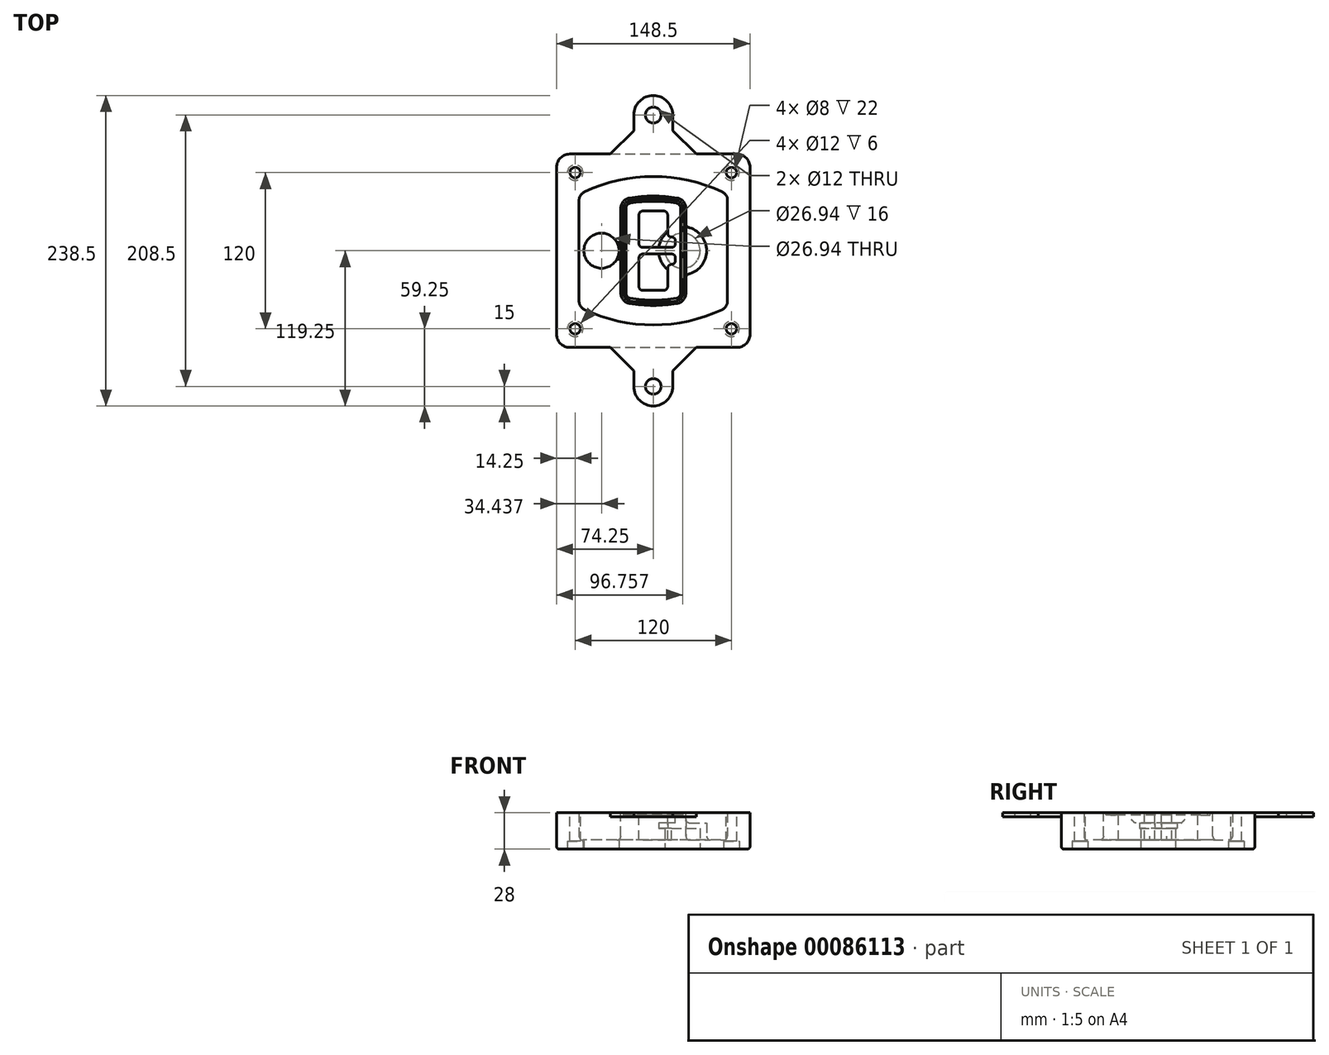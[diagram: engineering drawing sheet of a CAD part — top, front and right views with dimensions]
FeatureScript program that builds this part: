
annotation { "Feature Type Name" : "Feature", "Feature Type Description" : "" }
export const myFeature = defineFeature(function(context is Context, id is Id, definition is map)
    precondition{}
    {
        {
            var Q0;
            Q0=qCreatedBy(makeId("Top.planeOp"),FACE);
            var sketch = newSketch(context, id + "F0", { "sketchPlane" : qUnion([Q0])});
            skPoint(sketch, "E0.rect.middle", {"position": v(0, 0) * mm});
            skLineSegment(sketch, "E1.bottom", {"start": v(-64.25, -74.25) * mm, "end": v(64.25, -74.25) * mm});
            skLineSegment(sketch, "E1.top", {"start": v(-64.25, 74.25) * mm, "end": v(64.25, 74.25) * mm});
            skLineSegment(sketch, "E1.left", {"start": v(-74.25, -64.25) * mm, "end": v(-74.25, 64.25) * mm});
            skLineSegment(sketch, "E1.right", {"start": v(74.25, -64.25) * mm, "end": v(74.25, 64.25) * mm});
            skLineSegment(sketch, "E2", {"start": v(-74.25, 74.25) * mm, "end": v(74.25, -74.25) * mm, "construction": true});
            skLineSegment(sketch, "E3", {"start": v(74.25, 74.25) * mm, "end": v(-74.25, -74.25) * mm, "construction": true});
            skCircle(sketch, "E4", {"center": v(-60, 60) * mm, "radius": 4 * mm});
            skCircle(sketch, "E5", {"center": v(60, 60) * mm, "radius": 4 * mm});
            skCircle(sketch, "E6", {"center": v(60, -60) * mm, "radius": 4 * mm});
            skCircle(sketch, "E7", {"center": v(-60, -60) * mm, "radius": 4 * mm});
            skLineSegment(sketch, "E8", {"start": v(-60, 60) * mm, "end": v(60, 60) * mm, "construction": true});
            skLineSegment(sketch, "E9", {"start": v(60, 60) * mm, "end": v(60, -60) * mm, "construction": true});
            skLineSegment(sketch, "E10", {"start": v(60, -60) * mm, "end": v(-60, -60) * mm, "construction": true});
            skLineSegment(sketch, "E11", {"start": v(-60, -60) * mm, "end": v(-60, 60) * mm, "construction": true});
            skLineSegment(sketch, "E12", {"start": v(-60, 38.83) * mm, "end": v(-60, -38.83) * mm});
            skLineSegment(sketch, "E13", {"start": v(60, 38.83) * mm, "end": v(60, -38.83) * mm});
            skArc(sketch, "E14", {"start": v(54.26, 47.88) * mm, "mid": v(0, 60) * mm, "end": v(-54.26, 47.88) * mm});
            skArc(sketch, "E15", {"start": v(-54.26, -47.88) * mm, "mid": v(0, -60) * mm, "end": v(54.26, -47.88) * mm});
            skLineSegment(sketch, "E16", {"start": v(-60, 0) * mm, "end": v(60, 0) * mm, "construction": true});
            skPoint(sketch, "E17.visualSharp", {"position": v(-60, -45) * mm});
            skArc(sketch, "E17.filletArc", {"start": v(-60, -38.83) * mm, "mid": v(-58.44, -44.2) * mm, "end": v(-54.26, -47.88) * mm});
            skPoint(sketch, "E18.visualSharp", {"position": v(-60, 45) * mm});
            skArc(sketch, "E18.filletArc", {"start": v(-54.26, 47.88) * mm, "mid": v(-58.44, 44.2) * mm, "end": v(-60, 38.83) * mm});
            skPoint(sketch, "E19.visualSharp", {"position": v(60, 45) * mm});
            skArc(sketch, "E19.filletArc", {"start": v(60, 38.83) * mm, "mid": v(58.44, 44.2) * mm, "end": v(54.26, 47.88) * mm});
            skPoint(sketch, "E20.visualSharp", {"position": v(60, -45) * mm});
            skArc(sketch, "E20.filletArc", {"start": v(54.26, -47.88) * mm, "mid": v(58.44, -44.2) * mm, "end": v(60, -38.83) * mm});
            skPoint(sketch, "E21.visualSharp", {"position": v(-74.25, 74.25) * mm});
            skArc(sketch, "E21.filletArc", {"start": v(-64.25, 74.25) * mm, "mid": v(-71.32, 71.32) * mm, "end": v(-74.25, 64.25) * mm});
            skPoint(sketch, "E22.visualSharp", {"position": v(74.25, 74.25) * mm});
            skArc(sketch, "E22.filletArc", {"start": v(74.25, 64.25) * mm, "mid": v(71.32, 71.32) * mm, "end": v(64.25, 74.25) * mm});
            skPoint(sketch, "E23.visualSharp", {"position": v(74.25, -74.25) * mm});
            skArc(sketch, "E23.filletArc", {"start": v(64.25, -74.25) * mm, "mid": v(71.32, -71.32) * mm, "end": v(74.25, -64.25) * mm});
            skPoint(sketch, "E24.visualSharp", {"position": v(-74.25, -74.25) * mm});
            skArc(sketch, "E24.filletArc", {"start": v(-74.25, -64.25) * mm, "mid": v(-71.32, -71.32) * mm, "end": v(-64.25, -74.25) * mm});
            skArc(sketch, "E25.0", {"start": v(57, 38.83) * mm, "mid": v(55.9, 42.58) * mm, "end": v(52.98, 45.17) * mm});
            skLineSegment(sketch, "E25.1", {"start": v(57, 38.83) * mm, "end": v(57, -38.83) * mm});
            skArc(sketch, "E25.2", {"start": v(52.98, -45.17) * mm, "mid": v(55.9, -42.58) * mm, "end": v(57, -38.83) * mm});
            skArc(sketch, "E25.3", {"start": v(-52.98, -45.17) * mm, "mid": v(0, -57) * mm, "end": v(52.98, -45.17) * mm});
            skArc(sketch, "E25.4", {"start": v(-57, -38.83) * mm, "mid": v(-55.9, -42.58) * mm, "end": v(-52.98, -45.17) * mm});
            skArc(sketch, "E25.5", {"start": v(52.98, 45.17) * mm, "mid": v(0, 57) * mm, "end": v(-52.98, 45.17) * mm});
            skLineSegment(sketch, "E25.6", {"start": v(-57, 38.83) * mm, "end": v(-57, -38.83) * mm});
            skArc(sketch, "E25.7", {"start": v(-52.98, 45.17) * mm, "mid": v(-55.9, 42.58) * mm, "end": v(-57, 38.83) * mm});
            skArc(sketch, "E26.0", {"start": v(-55.96, 51.5) * mm, "mid": v(-61.82, 46.33) * mm, "end": v(-64, 38.83) * mm});
            skArc(sketch, "E26.1", {"start": v(55.96, 51.5) * mm, "mid": v(0, 64) * mm, "end": v(-55.96, 51.5) * mm});
            skArc(sketch, "E26.2", {"start": v(64, 38.83) * mm, "mid": v(61.82, 46.33) * mm, "end": v(55.96, 51.5) * mm});
            skLineSegment(sketch, "E26.3", {"start": v(64, 38.83) * mm, "end": v(64, -38.83) * mm});
            skArc(sketch, "E26.4", {"start": v(55.96, -51.5) * mm, "mid": v(61.82, -46.33) * mm, "end": v(64, -38.83) * mm});
            skLineSegment(sketch, "E26.5", {"start": v(-64, 38.83) * mm, "end": v(-64, -38.83) * mm});
            skArc(sketch, "E26.6", {"start": v(-55.96, -51.5) * mm, "mid": v(0, -64) * mm, "end": v(55.96, -51.5) * mm});
            skArc(sketch, "E26.7", {"start": v(-64, -38.83) * mm, "mid": v(-61.82, -46.33) * mm, "end": v(-55.96, -51.5) * mm});
            skSolve(sketch);
        }
        {
            var Q0;
            Q0=makeQuery(id+"F0.imprint","IMPRINT",FACE,{"disambiguationData":[TD([[makeQuery(id+"F0.imprint","IMPRINT",EDGE,{"derivedFrom":sQuery(id+"F0.wireOp",EDGE,"E1.bottom")}),1.0]])]});
            var Q1;
            Q1=makeQuery(id+"F0.imprint","IMPRINT",FACE,{"disambiguationData":[TD([[makeQuery(id+"F0.imprint","IMPRINT",EDGE,{"derivedFrom":sQuery(id+"F0.wireOp",EDGE,"E12")}),1.0]])]});
            var Q2;
            Q2=makeQuery(id+"F0.imprint","IMPRINT",FACE,{"disambiguationData":[TD([[makeQuery(id+"F0.imprint","IMPRINT",EDGE,{"derivedFrom":sQuery(id+"F0.wireOp",EDGE,"E25.0")}),1.0]])]});
            var Q3;
            Q3=makeQuery(id+"F0.imprint","IMPRINT",FACE,{"disambiguationData":[TD([[makeQuery(id+"F0.imprint","IMPRINT",EDGE,{"derivedFrom":sQuery(id+"F0.wireOp",EDGE,"E12")}),-1.0]])]});
            extrude(context, id + "F1", {"entities" : qUnion([Q0, Q1, Q2, Q3]), "oppositeDirection" : true, "depth" : 25 * mm});
        }
        {
            var Q0;
            Q0=makeQuery(id+"F0.imprint","IMPRINT",FACE,{"disambiguationData":[TD([[makeQuery(id+"F0.imprint","IMPRINT",EDGE,{"derivedFrom":sQuery(id+"F0.wireOp",EDGE,"E12")}),1.0]])]});
            extrude(context, id + "F2", {"entities" : qUnion([Q0]), "operationType" : NewBodyOperationType.ADD, "depth" : 3 * mm});
        }
        {
            var Q0;
            Q0=makeQuery(id+"F0.imprint","IMPRINT",FACE,{"disambiguationData":[TD([[makeQuery(id+"F0.imprint","IMPRINT",EDGE,{"derivedFrom":sQuery(id+"F0.wireOp",EDGE,"E25.0")}),1.0]])]});
            extrude(context, id + "F3", {"entities" : qUnion([Q0]), "operationType" : NewBodyOperationType.REMOVE, "oppositeDirection" : true, "depth" : 18 * mm});
        }
        {
            var Q0;
            Q0=makeQuery(id+"F2.opExtrude","CAP_FACE",FACE,{"disambiguationData":[OSD([sQuery(id+"F0.wireOp",EDGE,"E12"),sQuery(id+"F0.wireOp",EDGE,"E13"),sQuery(id+"F0.wireOp",EDGE,"E14"),sQuery(id+"F0.wireOp",EDGE,"E15"),sQuery(id+"F0.wireOp",EDGE,"E17.filletArc"),sQuery(id+"F0.wireOp",EDGE,"E18.filletArc"),sQuery(id+"F0.wireOp",EDGE,"E19.filletArc"),sQuery(id+"F0.wireOp",EDGE,"E20.filletArc"),sQuery(id+"F0.wireOp",EDGE,"E25.0"),sQuery(id+"F0.wireOp",EDGE,"E25.1"),sQuery(id+"F0.wireOp",EDGE,"E25.2"),sQuery(id+"F0.wireOp",EDGE,"E25.3"),sQuery(id+"F0.wireOp",EDGE,"E25.4"),sQuery(id+"F0.wireOp",EDGE,"E25.5"),sQuery(id+"F0.wireOp",EDGE,"E25.6"),sQuery(id+"F0.wireOp",EDGE,"E25.7")])],"isStart":false});
            var sketch = newSketch(context, id + "F4", { "sketchPlane" : qUnion([Q0])});
            skArc(sketch, "E27.0", {"start": v(-18.34, -40.45) * mm, "mid": v(0, -42) * mm, "end": v(18.34, -40.45) * mm});
            skArc(sketch, "E28.0", {"start": v(18.34, 40.45) * mm, "mid": v(0, 42) * mm, "end": v(-18.34, 40.45) * mm});
            skLineSegment(sketch, "E29", {"start": v(-25, 32.57) * mm, "end": v(-25, -32.57) * mm});
            skLineSegment(sketch, "E30", {"start": v(25, 32.57) * mm, "end": v(25, -32.57) * mm});
            skLineSegment(sketch, "E31", {"start": v(-25, 39.1) * mm, "end": v(25, 39.1) * mm, "construction": true});
            skLineSegment(sketch, "E32", {"start": v(-25, -39.1) * mm, "end": v(25, -39.1) * mm, "construction": true});
            skPoint(sketch, "E33.visualSharp", {"position": v(-25, 39.1) * mm});
            skArc(sketch, "E33.filletArc", {"start": v(-18.34, 40.45) * mm, "mid": v(-23.11, 37.73) * mm, "end": v(-25, 32.57) * mm});
            skPoint(sketch, "E34.visualSharp", {"position": v(25, 39.1) * mm});
            skArc(sketch, "E34.filletArc", {"start": v(25, 32.57) * mm, "mid": v(23.11, 37.73) * mm, "end": v(18.34, 40.45) * mm});
            skPoint(sketch, "E35.visualSharp", {"position": v(25, -39.1) * mm});
            skArc(sketch, "E35.filletArc", {"start": v(18.34, -40.45) * mm, "mid": v(23.11, -37.73) * mm, "end": v(25, -32.57) * mm});
            skPoint(sketch, "E36.visualSharp", {"position": v(-25, -39.1) * mm});
            skArc(sketch, "E36.filletArc", {"start": v(-25, -32.57) * mm, "mid": v(-23.11, -37.73) * mm, "end": v(-18.34, -40.45) * mm});
            skArc(sketch, "E37.0", {"start": v(52.98, 45.17) * mm, "mid": v(0, 57) * mm, "end": v(-52.98, 45.17) * mm});
            skArc(sketch, "E37.1", {"start": v(-52.98, 45.17) * mm, "mid": v(-55.9, 42.58) * mm, "end": v(-57, 38.83) * mm});
            skLineSegment(sketch, "E37.2", {"start": v(-57, 38.83) * mm, "end": v(-57, -38.83) * mm});
            skArc(sketch, "E37.3", {"start": v(-57, -38.83) * mm, "mid": v(-55.9, -42.58) * mm, "end": v(-52.98, -45.17) * mm});
            skArc(sketch, "E37.4", {"start": v(-52.98, -45.17) * mm, "mid": v(0, -57) * mm, "end": v(52.98, -45.17) * mm});
            skArc(sketch, "E37.5", {"start": v(52.98, -45.17) * mm, "mid": v(55.9, -42.58) * mm, "end": v(57, -38.83) * mm});
            skLineSegment(sketch, "E37.6", {"start": v(57, 38.83) * mm, "end": v(57, -38.83) * mm});
            skArc(sketch, "E37.7", {"start": v(57, 38.83) * mm, "mid": v(55.9, 42.58) * mm, "end": v(52.98, 45.17) * mm});
            skLineSegment(sketch, "E38.0", {"start": v(23, 32.57) * mm, "end": v(23, -32.57) * mm});
            skArc(sketch, "E38.1", {"start": v(18, -38.48) * mm, "mid": v(21.58, -36.44) * mm, "end": v(23, -32.57) * mm});
            skArc(sketch, "E38.2", {"start": v(-18, -38.48) * mm, "mid": v(0, -40) * mm, "end": v(18, -38.48) * mm});
            skArc(sketch, "E38.3", {"start": v(-23, -32.57) * mm, "mid": v(-21.58, -36.44) * mm, "end": v(-18, -38.48) * mm});
            skLineSegment(sketch, "E38.4", {"start": v(-23, 32.57) * mm, "end": v(-23, -32.57) * mm});
            skArc(sketch, "E38.5", {"start": v(23, 32.57) * mm, "mid": v(21.58, 36.44) * mm, "end": v(18, 38.48) * mm});
            skArc(sketch, "E38.6", {"start": v(-18, 38.48) * mm, "mid": v(-21.58, 36.44) * mm, "end": v(-23, 32.57) * mm});
            skArc(sketch, "E38.7", {"start": v(18, 38.48) * mm, "mid": v(0, 40) * mm, "end": v(-18, 38.48) * mm});
            skArc(sketch, "E39.0", {"start": v(21, 32.57) * mm, "mid": v(20.06, 35.15) * mm, "end": v(17.67, 36.5) * mm});
            skLineSegment(sketch, "E39.1", {"start": v(21, 32.57) * mm, "end": v(21, -32.57) * mm});
            skArc(sketch, "E39.2", {"start": v(17.67, -36.5) * mm, "mid": v(20.06, -35.15) * mm, "end": v(21, -32.57) * mm});
            skArc(sketch, "E39.3", {"start": v(-17.67, -36.5) * mm, "mid": v(0, -38) * mm, "end": v(17.67, -36.5) * mm});
            skArc(sketch, "E39.4", {"start": v(-21, -32.57) * mm, "mid": v(-20.06, -35.15) * mm, "end": v(-17.67, -36.5) * mm});
            skArc(sketch, "E39.5", {"start": v(17.67, 36.5) * mm, "mid": v(0, 38) * mm, "end": v(-17.67, 36.5) * mm});
            skLineSegment(sketch, "E39.6", {"start": v(-21, 32.57) * mm, "end": v(-21, -32.57) * mm});
            skArc(sketch, "E39.7", {"start": v(-17.67, 36.5) * mm, "mid": v(-20.06, 35.15) * mm, "end": v(-21, 32.57) * mm});
            skLineSegment(sketch, "E40", {"start": v(-25, 0) * mm, "end": v(25, 0) * mm, "construction": true});
            skLineSegment(sketch, "E41", {"start": v(-11, 5.5) * mm, "end": v(-11, 27.5) * mm});
            skLineSegment(sketch, "E42", {"start": v(-8, 30.5) * mm, "end": v(8, 30.5) * mm});
            skLineSegment(sketch, "E43", {"start": v(11, 27.5) * mm, "end": v(11, 13.5) * mm});
            skLineSegment(sketch, "E44", {"start": v(14, 10.5) * mm, "end": v(14, 10.5) * mm});
            skLineSegment(sketch, "E45", {"start": v(17, 7.5) * mm, "end": v(17, 5.5) * mm});
            skLineSegment(sketch, "E46", {"start": v(14, 2.5) * mm, "end": v(-8, 2.5) * mm});
            skPoint(sketch, "E47.visualSharp", {"position": v(-11, 30.5) * mm});
            skArc(sketch, "E47.filletArc", {"start": v(-8, 30.5) * mm, "mid": v(-10.12, 29.62) * mm, "end": v(-11, 27.5) * mm});
            skPoint(sketch, "E48.visualSharp", {"position": v(11, 30.5) * mm});
            skArc(sketch, "E48.filletArc", {"start": v(11, 27.5) * mm, "mid": v(10.12, 29.62) * mm, "end": v(8, 30.5) * mm});
            skPoint(sketch, "E49.visualSharp", {"position": v(11, 10.5) * mm});
            skArc(sketch, "E49.filletArc", {"start": v(11, 13.5) * mm, "mid": v(11.88, 11.38) * mm, "end": v(14, 10.5) * mm});
            skPoint(sketch, "E50.visualSharp", {"position": v(17, 10.5) * mm});
            skArc(sketch, "E50.filletArc", {"start": v(17, 7.5) * mm, "mid": v(16.12, 9.62) * mm, "end": v(14, 10.5) * mm});
            skPoint(sketch, "E51.visualSharp", {"position": v(17, 2.5) * mm});
            skArc(sketch, "E51.filletArc", {"start": v(14, 2.5) * mm, "mid": v(16.12, 3.38) * mm, "end": v(17, 5.5) * mm});
            skPoint(sketch, "E52.visualSharp", {"position": v(-11, 2.5) * mm});
            skArc(sketch, "E52.filletArc", {"start": v(-11, 5.5) * mm, "mid": v(-10.12, 3.38) * mm, "end": v(-8, 2.5) * mm});
            skLineSegment(sketch, "E53.0.MirrorCS", {"start": v(14, -2.5) * mm, "end": v(-8, -2.5) * mm});
            skArc(sketch, "E54.0.MirrorCS", {"start": v(-11, -5.5) * mm, "mid": v(-10.12, -3.38) * mm, "end": v(-8, -2.5) * mm});
            skLineSegment(sketch, "E55.0.MirrorCS", {"start": v(-11, -5.5) * mm, "end": v(-11, -27.5) * mm});
            skArc(sketch, "E56.0.MirrorCS", {"start": v(-8, -30.5) * mm, "mid": v(-10.12, -29.62) * mm, "end": v(-11, -27.5) * mm});
            skLineSegment(sketch, "E57.0.MirrorCS", {"start": v(-8, -30.5) * mm, "end": v(8, -30.5) * mm});
            skArc(sketch, "E58.0.MirrorCS", {"start": v(11, -27.5) * mm, "mid": v(10.12, -29.62) * mm, "end": v(8, -30.5) * mm});
            skLineSegment(sketch, "E59.0.MirrorCS", {"start": v(11, -27.5) * mm, "end": v(11, -13.5) * mm});
            skArc(sketch, "E60.0.MirrorCS", {"start": v(11, -13.5) * mm, "mid": v(11.88, -11.38) * mm, "end": v(14, -10.5) * mm});
            skArc(sketch, "E61.0.MirrorCS", {"start": v(17, -7.5) * mm, "mid": v(16.12, -9.62) * mm, "end": v(14, -10.5) * mm});
            skLineSegment(sketch, "E62.0.MirrorCS", {"start": v(17, -7.5) * mm, "end": v(17, -5.5) * mm});
            skArc(sketch, "E63.0.MirrorCS", {"start": v(14, -2.5) * mm, "mid": v(16.12, -3.38) * mm, "end": v(17, -5.5) * mm});
            skSolve(sketch);
        }
        {
            var Q0;
            Q0=makeQuery(id+"F4.imprint","IMPRINT",FACE,{"disambiguationData":[TD([[makeQuery(id+"F4.imprint","IMPRINT",EDGE,{"derivedFrom":sQuery(id+"F4.wireOp",EDGE,"E27.0")}),1.0]])]});
            var Q1;
            Q1=makeQuery(id+"F4.imprint","IMPRINT",FACE,{"disambiguationData":[TD([[makeQuery(id+"F4.imprint","IMPRINT",EDGE,{"derivedFrom":sQuery(id+"F4.wireOp",EDGE,"E38.0")}),-1.0]])]});
            var Q2;
            Q2=makeQuery(id+"F4.imprint","IMPRINT",FACE,{"disambiguationData":[TD([[makeQuery(id+"F4.imprint","IMPRINT",EDGE,{"derivedFrom":sQuery(id+"F4.wireOp",EDGE,"E39.0")}),1.0]])]});
            extrude(context, id + "F5", {"entities" : qUnion([Q0, Q1, Q2]), "operationType" : NewBodyOperationType.ADD, "endBound" : BoundingType.UP_TO_NEXT, "oppositeDirection" : true, "depth" : 25 * mm});
        }
        {
            var Q0;
            Q0=makeQuery(id+"F4.imprint","IMPRINT",FACE,{"disambiguationData":[TD([[makeQuery(id+"F4.imprint","IMPRINT",EDGE,{"derivedFrom":sQuery(id+"F4.wireOp",EDGE,"E38.0")}),-1.0]])]});
            extrude(context, id + "F6", {"entities" : qUnion([Q0]), "operationType" : NewBodyOperationType.REMOVE, "oppositeDirection" : true, "depth" : 2 * mm});
        }
        {
            var Q0;
            Q0=makeQuery(id+"F1.opExtrude","CAP_FACE",FACE,{"disambiguationData":[OSD([sQuery(id+"F0.wireOp",EDGE,"E1.bottom"),sQuery(id+"F0.wireOp",EDGE,"E1.top"),sQuery(id+"F0.wireOp",EDGE,"E1.left"),sQuery(id+"F0.wireOp",EDGE,"E1.right"),sQuery(id+"F0.wireOp",EDGE,"E4"),sQuery(id+"F0.wireOp",EDGE,"E5"),sQuery(id+"F0.wireOp",EDGE,"E6"),sQuery(id+"F0.wireOp",EDGE,"E7"),sQuery(id+"F0.wireOp",EDGE,"E21.filletArc"),sQuery(id+"F0.wireOp",EDGE,"E22.filletArc"),sQuery(id+"F0.wireOp",EDGE,"E23.filletArc"),sQuery(id+"F0.wireOp",EDGE,"E24.filletArc")])],"isStart":false});
            var sketch = newSketch(context, id + "F7", { "sketchPlane" : qUnion([Q0])});
            skCircle(sketch, "E64", {"center": v(22.5, 0) * mm, "radius": 13.47 * mm});
            skCircle(sketch, "E65", {"center": v(-39.81, 0) * mm, "radius": 13.47 * mm});
            skLineSegment(sketch, "E66", {"start": v(74.25, 0) * mm, "end": v(-74.25, 0) * mm});
            skCircle(sketch, "E67", {"center": v(22.5, 0) * mm, "radius": 18.47 * mm});
            skCircle(sketch, "E68", {"center": v(60, -60) * mm, "radius": 6 * mm});
            skCircle(sketch, "E69", {"center": v(-60, -60) * mm, "radius": 6 * mm});
            skCircle(sketch, "E70", {"center": v(-60, 60) * mm, "radius": 6 * mm});
            skCircle(sketch, "E71", {"center": v(60, 60) * mm, "radius": 6 * mm});
            skSolve(sketch);
        }
        {
            var Q0;
            {var subQ1=sQuery(id+"F7.wireOp",EDGE,"E66");var subQ4=sQuery(id+"F7.wireOp",EDGE,"E64");var subQ6=makeQuery(id+"F7.imprint","INTERSECT",VERTEX,{"disambiguationData":[OD(0.0)],"derivedFrom":[subQ4,subQ1]});Q0=makeQuery(id+"F7.imprint","IMPRINT",FACE,{"disambiguationData":[TD([[makeQuery(id+"F7.imprint","IMPRINT",EDGE,{"disambiguationData":[TD([[subQ6,-1.0]])],"derivedFrom":subQ4}),-1.0]])]});}
            var Q1;
            {var subQ0=sQuery(id+"F7.wireOp",EDGE,"E66");var subQ1=sQuery(id+"F7.wireOp",EDGE,"E64");var subQ3=makeQuery(id+"F7.imprint","INTERSECT",VERTEX,{"disambiguationData":[OD(0.0)],"derivedFrom":[subQ1,subQ0]});Q1=makeQuery(id+"F7.imprint","IMPRINT",FACE,{"disambiguationData":[TD([[makeQuery(id+"F7.imprint","IMPRINT",EDGE,{"disambiguationData":[TD([[subQ3,-1.0]])],"derivedFrom":subQ1}),1.0]])]});}
            var Q2;
            {var subQ0=sQuery(id+"F7.wireOp",EDGE,"E66");var subQ1=sQuery(id+"F7.wireOp",EDGE,"E64");var subQ3=makeQuery(id+"F7.imprint","INTERSECT",VERTEX,{"disambiguationData":[OD(0.0)],"derivedFrom":[subQ1,subQ0]});Q2=makeQuery(id+"F7.imprint","IMPRINT",FACE,{"disambiguationData":[TD([[makeQuery(id+"F7.imprint","IMPRINT",EDGE,{"disambiguationData":[TD([[subQ3,1.0]])],"derivedFrom":subQ1}),1.0]])]});}
            var Q3;
            {var subQ1=sQuery(id+"F7.wireOp",EDGE,"E66");var subQ4=sQuery(id+"F7.wireOp",EDGE,"E64");var subQ6=makeQuery(id+"F7.imprint","INTERSECT",VERTEX,{"disambiguationData":[OD(0.0)],"derivedFrom":[subQ4,subQ1]});Q3=makeQuery(id+"F7.imprint","IMPRINT",FACE,{"disambiguationData":[TD([[makeQuery(id+"F7.imprint","IMPRINT",EDGE,{"disambiguationData":[TD([[subQ6,1.0]])],"derivedFrom":subQ4}),-1.0]])]});}
            extrude(context, id + "F8", {"entities" : qUnion([Q0, Q1, Q2, Q3]), "operationType" : NewBodyOperationType.ADD, "oppositeDirection" : true, "depth" : 20 * mm});
        }
        {
            var Q0;
            {var subQ0=sQuery(id+"F7.wireOp",EDGE,"E66");var subQ1=sQuery(id+"F7.wireOp",EDGE,"E64");var subQ3=makeQuery(id+"F7.imprint","INTERSECT",VERTEX,{"disambiguationData":[OD(0.0)],"derivedFrom":[subQ1,subQ0]});Q0=makeQuery(id+"F7.imprint","IMPRINT",FACE,{"disambiguationData":[TD([[makeQuery(id+"F7.imprint","IMPRINT",EDGE,{"disambiguationData":[TD([[subQ3,-1.0]])],"derivedFrom":subQ1}),1.0]])]});}
            var Q1;
            {var subQ0=sQuery(id+"F7.wireOp",EDGE,"E66");var subQ1=sQuery(id+"F7.wireOp",EDGE,"E64");var subQ3=makeQuery(id+"F7.imprint","INTERSECT",VERTEX,{"disambiguationData":[OD(0.0)],"derivedFrom":[subQ1,subQ0]});Q1=makeQuery(id+"F7.imprint","IMPRINT",FACE,{"disambiguationData":[TD([[makeQuery(id+"F7.imprint","IMPRINT",EDGE,{"disambiguationData":[TD([[subQ3,1.0]])],"derivedFrom":subQ1}),1.0]])]});}
            extrude(context, id + "F9", {"entities" : qUnion([Q0, Q1]), "operationType" : NewBodyOperationType.REMOVE, "oppositeDirection" : true, "depth" : 16 * mm});
        }
        {
            var Q0;
            {var subQ0=sQuery(id+"F7.wireOp",EDGE,"E66");var subQ1=sQuery(id+"F7.wireOp",EDGE,"E65");var subQ3=makeQuery(id+"F7.imprint","INTERSECT",VERTEX,{"disambiguationData":[OD(0.0)],"derivedFrom":[subQ1,subQ0]});Q0=makeQuery(id+"F7.imprint","IMPRINT",FACE,{"disambiguationData":[TD([[makeQuery(id+"F7.imprint","IMPRINT",EDGE,{"disambiguationData":[TD([[subQ3,-1.0]])],"derivedFrom":subQ1}),1.0]])]});}
            var Q1;
            {var subQ0=sQuery(id+"F7.wireOp",EDGE,"E66");var subQ1=sQuery(id+"F7.wireOp",EDGE,"E65");var subQ3=makeQuery(id+"F7.imprint","INTERSECT",VERTEX,{"disambiguationData":[OD(0.0)],"derivedFrom":[subQ1,subQ0]});Q1=makeQuery(id+"F7.imprint","IMPRINT",FACE,{"disambiguationData":[TD([[makeQuery(id+"F7.imprint","IMPRINT",EDGE,{"disambiguationData":[TD([[subQ3,1.0]])],"derivedFrom":subQ1}),1.0]])]});}
            extrude(context, id + "F10", {"entities" : qUnion([Q0, Q1]), "operationType" : NewBodyOperationType.REMOVE, "oppositeDirection" : true, "depth" : 25 * mm});
        }
        {
            var Q0;
            Q0=makeQuery(id+"F7.imprint","IMPRINT",FACE,{"disambiguationData":[TD([[makeQuery(id+"F7.imprint","IMPRINT",EDGE,{"derivedFrom":sQuery(id+"F7.wireOp",EDGE,"E68")}),1.0]])]});
            var Q1;
            Q1=makeQuery(id+"F7.imprint","IMPRINT",FACE,{"disambiguationData":[TD([[makeQuery(id+"F7.imprint","IMPRINT",EDGE,{"derivedFrom":makeQuery(id+"F1.opExtrude","CAP_EDGE",EDGE,{"disambiguationData":[OSD([sQuery(id+"F0.wireOp",EDGE,"E5")])],"isStart":false})}),-1.0]])]});
            var Q2;
            Q2=makeQuery(id+"F7.imprint","IMPRINT",FACE,{"disambiguationData":[TD([[makeQuery(id+"F7.imprint","IMPRINT",EDGE,{"derivedFrom":sQuery(id+"F7.wireOp",EDGE,"E69")}),1.0]])]});
            var Q3;
            Q3=makeQuery(id+"F7.imprint","IMPRINT",FACE,{"disambiguationData":[TD([[makeQuery(id+"F7.imprint","IMPRINT",EDGE,{"derivedFrom":makeQuery(id+"F1.opExtrude","CAP_EDGE",EDGE,{"disambiguationData":[OSD([sQuery(id+"F0.wireOp",EDGE,"E4")])],"isStart":false})}),-1.0]])]});
            var Q4;
            Q4=makeQuery(id+"F7.imprint","IMPRINT",FACE,{"disambiguationData":[TD([[makeQuery(id+"F7.imprint","IMPRINT",EDGE,{"derivedFrom":sQuery(id+"F7.wireOp",EDGE,"E70")}),1.0]])]});
            var Q5;
            Q5=makeQuery(id+"F7.imprint","IMPRINT",FACE,{"disambiguationData":[TD([[makeQuery(id+"F7.imprint","IMPRINT",EDGE,{"derivedFrom":makeQuery(id+"F1.opExtrude","CAP_EDGE",EDGE,{"disambiguationData":[OSD([sQuery(id+"F0.wireOp",EDGE,"E7")])],"isStart":false})}),-1.0]])]});
            var Q6;
            Q6=makeQuery(id+"F7.imprint","IMPRINT",FACE,{"disambiguationData":[TD([[makeQuery(id+"F7.imprint","IMPRINT",EDGE,{"derivedFrom":sQuery(id+"F7.wireOp",EDGE,"E71")}),1.0]])]});
            var Q7;
            Q7=makeQuery(id+"F7.imprint","IMPRINT",FACE,{"disambiguationData":[TD([[makeQuery(id+"F7.imprint","IMPRINT",EDGE,{"derivedFrom":makeQuery(id+"F1.opExtrude","CAP_EDGE",EDGE,{"disambiguationData":[OSD([sQuery(id+"F0.wireOp",EDGE,"E6")])],"isStart":false})}),-1.0]])]});
            extrude(context, id + "F11", {"entities" : qUnion([Q0, Q1, Q2, Q3, Q4, Q5, Q6, Q7]), "operationType" : NewBodyOperationType.REMOVE, "oppositeDirection" : true, "depth" : 6 * mm});
        }
        {
            var Q0;
            Q0=makeQuery(id+"F9.boolean.opBoolean","COPY",FACE,{"derivedFrom":makeQuery(id+"F9.opExtrude","CAP_FACE",FACE,{"disambiguationData":[OSD([sQuery(id+"F7.wireOp",EDGE,"E64")])],"isStart":false})});
            var sketch = newSketch(context, id + "F12", { "sketchPlane" : qUnion([Q0])});
            skArc(sketch, "E72.0", {"start": v(11, 14.45) * mm, "mid": v(6.45, 9.13) * mm, "end": v(4.2, 2.5) * mm});
            skArc(sketch, "E72.1", {"start": v(4.2, -2.5) * mm, "mid": v(6.45, -9.13) * mm, "end": v(11, -14.45) * mm});
            skLineSegment(sketch, "E73", {"start": v(4.2, -2.5) * mm, "end": v(14, -2.5) * mm});
            skLineSegment(sketch, "E74.0", {"start": v(14, 2.5) * mm, "end": v(4.2, 2.5) * mm});
            skArc(sketch, "E74.1", {"start": v(14, 2.5) * mm, "mid": v(16.12, 3.38) * mm, "end": v(17, 5.5) * mm});
            skLineSegment(sketch, "E74.2", {"start": v(17, 7.5) * mm, "end": v(17, 5.5) * mm});
            skArc(sketch, "E74.3", {"start": v(17, 7.5) * mm, "mid": v(16.12, 9.62) * mm, "end": v(14, 10.5) * mm});
            skArc(sketch, "E74.4", {"start": v(11, 13.5) * mm, "mid": v(11.88, 11.38) * mm, "end": v(14, 10.5) * mm});
            skLineSegment(sketch, "E74.5", {"start": v(11, 14.45) * mm, "end": v(11, 13.5) * mm});
            skLineSegment(sketch, "E74.7", {"start": v(14, -2.5) * mm, "end": v(4.2, -2.5) * mm});
            skArc(sketch, "E74.8", {"start": v(14, -2.5) * mm, "mid": v(16.12, -3.38) * mm, "end": v(17, -5.5) * mm});
            skLineSegment(sketch, "E74.9", {"start": v(17, -7.5) * mm, "end": v(17, -5.5) * mm});
            skArc(sketch, "E74.10", {"start": v(17, -7.5) * mm, "mid": v(16.12, -9.62) * mm, "end": v(14, -10.5) * mm});
            skArc(sketch, "E74.11", {"start": v(11, -13.5) * mm, "mid": v(11.88, -11.38) * mm, "end": v(14, -10.5) * mm});
            skLineSegment(sketch, "E74.12", {"start": v(11, -14.45) * mm, "end": v(11, -13.5) * mm});
            skPoint(sketch, "E75.orphan", {"position": v(11, -27.5) * mm});
            skPoint(sketch, "E76.orphan", {"position": v(-8, -2.5) * mm});
            skPoint(sketch, "E77.orphan", {"position": v(-8, 2.5) * mm});
            skPoint(sketch, "E78.orphan", {"position": v(11, 27.5) * mm});
            skSolve(sketch);
        }
        {
            var Q0;
            {var subQ7=sQuery(id+"F12.wireOp",EDGE,"E72.0");var subQ14=sQuery(id+"F12.wireOp",EDGE,"E72.1");var subQ16=sQuery(id+"F12.wireOp",EDGE,"E74.1");var subQ18=sQuery(id+"F12.wireOp",EDGE,"E74.8");Q0=qUnion([makeQuery(id+"F12.imprint","IMPRINT",FACE,{"disambiguationData":[TD([[makeQuery(id+"F12.imprint","IMPRINT",EDGE,{"derivedFrom":subQ7}),1.0]])]}),makeQuery(id+"F12.imprint","IMPRINT",FACE,{"disambiguationData":[TD([[makeQuery(id+"F12.imprint","IMPRINT",EDGE,{"derivedFrom":subQ14}),1.0]])]}),makeQuery(id+"F12.imprint","IMPRINT",FACE,{"disambiguationData":[TD([[makeQuery(id+"F12.imprint","IMPRINT",EDGE,{"derivedFrom":subQ16}),1.0]])]}),makeQuery(id+"F12.imprint","IMPRINT",FACE,{"disambiguationData":[TD([[makeQuery(id+"F12.imprint","IMPRINT",EDGE,{"derivedFrom":subQ18}),-1.0]])]})]);}
            var Q1;
            Q1=makeQuery(id+"F5.boolean.opBoolean","SPLIT",FACE,{"disambiguationData":[TD([makeQuery(id+"F5.opExtrude","SWEPT_FACE",FACE,{"disambiguationData":[OSD([sQuery(id+"F4.wireOp",EDGE,"E41")])]})])],"derivedFrom":makeQuery(id+"F3.boolean.opBoolean","COPY",FACE,{"derivedFrom":makeQuery(id+"F3.opExtrude","CAP_FACE",FACE,{"disambiguationData":[OSD([sQuery(id+"F0.wireOp",EDGE,"E25.0"),sQuery(id+"F0.wireOp",EDGE,"E25.1"),sQuery(id+"F0.wireOp",EDGE,"E25.2"),sQuery(id+"F0.wireOp",EDGE,"E25.3"),sQuery(id+"F0.wireOp",EDGE,"E25.4"),sQuery(id+"F0.wireOp",EDGE,"E25.5"),sQuery(id+"F0.wireOp",EDGE,"E25.6"),sQuery(id+"F0.wireOp",EDGE,"E25.7")])],"isStart":false})})});
            extrude(context, id + "F13", {"entities" : qUnion([Q0]), "operationType" : NewBodyOperationType.REMOVE, "endBound" : BoundingType.UP_TO_SURFACE, "endBoundEntityFace" : qUnion([Q1]), "depth" : 25 * mm});
        }
        {
            var Q0;
            Q0=makeQuery(id+"F3.boolean.opBoolean","COPY",EDGE,{"derivedFrom":makeQuery(id+"F3.opExtrude","CAP_EDGE",EDGE,{"disambiguationData":[OSD([sQuery(id+"F0.wireOp",EDGE,"E25.6")])],"isStart":false})});
            var Q1;
            Q1=makeQuery(id+"F8.boolean.opBoolean","INTERSECT",EDGE,{"derivedFrom":[makeQuery(id+"F5.opExtrude","SWEPT_FACE",FACE,{"disambiguationData":[OSD([sQuery(id+"F4.wireOp",EDGE,"E30")])]}),makeQuery(id+"F8.opExtrude","CAP_FACE",FACE,{"disambiguationData":[OSD([sQuery(id+"F7.wireOp",EDGE,"E67")])],"isStart":false})]});
            var Q2;
            Q2=makeQuery(id+"F8.boolean.opBoolean","INTERSECT",EDGE,{"disambiguationData":[OD(1.0)],"derivedFrom":[makeQuery(id+"F5.opExtrude","SWEPT_FACE",FACE,{"disambiguationData":[OSD([sQuery(id+"F4.wireOp",EDGE,"E30")])]}),makeQuery(id+"F8.opExtrude","SWEPT_FACE",FACE,{"disambiguationData":[OSD([sQuery(id+"F7.wireOp",EDGE,"E67")])]})]});
            var Q3;
            {var subQ0=sQuery(id+"F4.wireOp",EDGE,"E30");Q3=makeQuery(id+"F8.boolean.opBoolean","SPLIT",EDGE,{"disambiguationData":[TD([makeQuery(id+"F5.opExtrude","SWEPT_FACE",FACE,{"disambiguationData":[OSD([sQuery(id+"F4.wireOp",EDGE,"E35.filletArc")])]})])],"derivedFrom":makeQuery(id+"F5.opExtrude","CAP_EDGE",EDGE,{"disambiguationData":[OSD([subQ0])],"isStart":false})});}
            var Q4;
            {var subQ0=sQuery(id+"F0.wireOp",EDGE,"E25.7");var subQ1=sQuery(id+"F0.wireOp",EDGE,"E25.1");var subQ2=sQuery(id+"F0.wireOp",EDGE,"E25.6");var subQ3=sQuery(id+"F0.wireOp",EDGE,"E25.5");var subQ4=sQuery(id+"F0.wireOp",EDGE,"E25.4");var subQ5=sQuery(id+"F0.wireOp",EDGE,"E25.0");var subQ6=sQuery(id+"F0.wireOp",EDGE,"E25.2");var subQ7=sQuery(id+"F0.wireOp",EDGE,"E25.3");Q4=makeQuery(id+"F8.boolean.opBoolean","INTERSECT",EDGE,{"derivedFrom":[makeQuery(id+"F5.boolean.opBoolean","SPLIT",FACE,{"disambiguationData":[TD([makeQuery(id+"F2.opExtrude","SWEPT_FACE",FACE,{"disambiguationData":[OSD([subQ5])]})])],"derivedFrom":makeQuery(id+"F3.boolean.opBoolean","COPY",FACE,{"derivedFrom":makeQuery(id+"F3.opExtrude","CAP_FACE",FACE,{"disambiguationData":[OSD([subQ5,subQ1,subQ6,subQ7,subQ4,subQ3,subQ2,subQ0])],"isStart":false})})}),makeQuery(id+"F8.opExtrude","SWEPT_FACE",FACE,{"disambiguationData":[OSD([sQuery(id+"F7.wireOp",EDGE,"E67")])]})]});}
            var Q5;
            Q5=makeQuery(id+"F8.boolean.opBoolean","INTERSECT",EDGE,{"disambiguationData":[OD(0.0)],"derivedFrom":[makeQuery(id+"F5.opExtrude","SWEPT_FACE",FACE,{"disambiguationData":[OSD([sQuery(id+"F4.wireOp",EDGE,"E30")])]}),makeQuery(id+"F8.opExtrude","SWEPT_FACE",FACE,{"disambiguationData":[OSD([sQuery(id+"F7.wireOp",EDGE,"E67")])]})]});
            fillet(context, id + "F14", {"entities" : qUnion([Q0, Q1, Q2, Q3, Q4, Q5]), "radius" : 3 * mm, "tangentPropagation" : true, "allowEdgeOverflow" : false});
        }
        {
            var Q0;
            Q0=makeQuery(id+"F1.opExtrude","CAP_EDGE",EDGE,{"disambiguationData":[OSD([sQuery(id+"F0.wireOp",EDGE,"E1.bottom")])],"isStart":false});
            fillet(context, id + "F15", {"entities" : qUnion([Q0]), "radius" : 2 * mm, "tangentPropagation" : true, "allowEdgeOverflow" : false});
        }
        {
            var Q0;
            {var subQ0=sQuery(id+"F0.wireOp",EDGE,"E22.filletArc");var subQ1=sQuery(id+"F0.wireOp",EDGE,"E7");var subQ2=sQuery(id+"F0.wireOp",EDGE,"E6");var subQ3=sQuery(id+"F0.wireOp",EDGE,"E5");var subQ4=sQuery(id+"F0.wireOp",EDGE,"E4");var subQ5=sQuery(id+"F0.wireOp",EDGE,"E1.bottom");var subQ6=sQuery(id+"F0.wireOp",EDGE,"E21.filletArc");var subQ7=sQuery(id+"F0.wireOp",EDGE,"E1.top");var subQ8=sQuery(id+"F0.wireOp",EDGE,"E1.left");var subQ9=sQuery(id+"F0.wireOp",EDGE,"E1.right");var subQ10=sQuery(id+"F0.wireOp",EDGE,"E23.filletArc");var subQ11=sQuery(id+"F0.wireOp",EDGE,"E24.filletArc");Q0=makeQuery(id+"F2.boolean.opBoolean","SPLIT",FACE,{"disambiguationData":[TD([makeQuery(id+"F1.opExtrude","SWEPT_FACE",FACE,{"disambiguationData":[OSD([subQ5])]})])],"derivedFrom":makeQuery(id+"F1.opExtrude","CAP_FACE",FACE,{"disambiguationData":[OSD([subQ5,subQ7,subQ8,subQ9,subQ4,subQ3,subQ2,subQ1,subQ6,subQ0,subQ10,subQ11])],"isStart":true})});}
            var sketch = newSketch(context, id + "F16", { "sketchPlane" : qUnion([Q0])});
            skLineSegment(sketch, "E79", {"start": v(0, 74.25) * mm, "end": v(0, 104.25) * mm, "construction": true});
            skCircle(sketch, "E80", {"center": v(0, 104.25) * mm, "radius": 6 * mm});
            skArc(sketch, "E81", {"start": v(-15, 104.25) * mm, "mid": v(0, 119.25) * mm, "end": v(15, 104.25) * mm});
            skLineSegment(sketch, "E82", {"start": v(-15, 104.25) * mm, "end": v(-15, 92.25) * mm});
            skLineSegment(sketch, "E83", {"start": v(15, 104.25) * mm, "end": v(15, 92.25) * mm});
            skLineSegment(sketch, "E84", {"start": v(-15, 92.25) * mm, "end": v(-33, 74.25) * mm});
            skLineSegment(sketch, "E85", {"start": v(15, 92.25) * mm, "end": v(33, 74.25) * mm});
            skLineSegment(sketch, "E86.MirrorCS", {"start": v(15, -92.25) * mm, "end": v(33, -74.25) * mm});
            skLineSegment(sketch, "E87.MirrorCS", {"start": v(15, -104.25) * mm, "end": v(15, -92.25) * mm});
            skArc(sketch, "E88.MirrorCS", {"start": v(-15, -104.25) * mm, "mid": v(0, -119.25) * mm, "end": v(15, -104.25) * mm});
            skCircle(sketch, "E89.MirrorC", {"center": v(0, -104.25) * mm, "radius": 6 * mm});
            skLineSegment(sketch, "E90.MirrorCS", {"start": v(-15, -92.25) * mm, "end": v(-33, -74.25) * mm});
            skLineSegment(sketch, "E91.MirrorCS", {"start": v(-15, -104.25) * mm, "end": v(-15, -92.25) * mm});
            skSolve(sketch);
        }
        {
            var Q0;
            Q0=makeQuery(id+"F16.imprint","IMPRINT",FACE,{"disambiguationData":[TD([[makeQuery(id+"F16.imprint","IMPRINT",EDGE,{"derivedFrom":sQuery(id+"F16.wireOp",EDGE,"E80")}),-1.0]])]});
            var Q1;
            {var subQ0=sQuery(id+"F16.wireOp",EDGE,"E86.MirrorCS");Q1=makeQuery(id+"F16.imprint","IMPRINT",FACE,{"disambiguationData":[TD([[makeQuery(id+"F16.imprint","IMPRINT",EDGE,{"derivedFrom":subQ0}),1.0]])]});}
            var Q2;
            Q2=makeQuery(id+"F16.imprint","IMPRINT",FACE,{"disambiguationData":[TD([[makeQuery(id+"F16.imprint","IMPRINT",EDGE,{"derivedFrom":makeQuery(id+"F1.opExtrude","CAP_EDGE",EDGE,{"disambiguationData":[OSD([sQuery(id+"F0.wireOp",EDGE,"E1.left")])],"isStart":true})}),-1.0]])]});
            var Q3;
            Q3=makeQuery(id+"F2.opExtrude","CAP_FACE",FACE,{"disambiguationData":[OSD([sQuery(id+"F0.wireOp",EDGE,"E12"),sQuery(id+"F0.wireOp",EDGE,"E13"),sQuery(id+"F0.wireOp",EDGE,"E14"),sQuery(id+"F0.wireOp",EDGE,"E15"),sQuery(id+"F0.wireOp",EDGE,"E17.filletArc"),sQuery(id+"F0.wireOp",EDGE,"E18.filletArc"),sQuery(id+"F0.wireOp",EDGE,"E19.filletArc"),sQuery(id+"F0.wireOp",EDGE,"E20.filletArc"),sQuery(id+"F0.wireOp",EDGE,"E25.0"),sQuery(id+"F0.wireOp",EDGE,"E25.1"),sQuery(id+"F0.wireOp",EDGE,"E25.2"),sQuery(id+"F0.wireOp",EDGE,"E25.3"),sQuery(id+"F0.wireOp",EDGE,"E25.4"),sQuery(id+"F0.wireOp",EDGE,"E25.5"),sQuery(id+"F0.wireOp",EDGE,"E25.6"),sQuery(id+"F0.wireOp",EDGE,"E25.7")])],"isStart":false});
            extrude(context, id + "F17", {"entities" : qUnion([Q0, Q1, Q2]), "operationType" : NewBodyOperationType.ADD, "endBound" : BoundingType.UP_TO_SURFACE, "endBoundEntityFace" : qUnion([Q3]), "depth" : 25 * mm});
        }
    });
